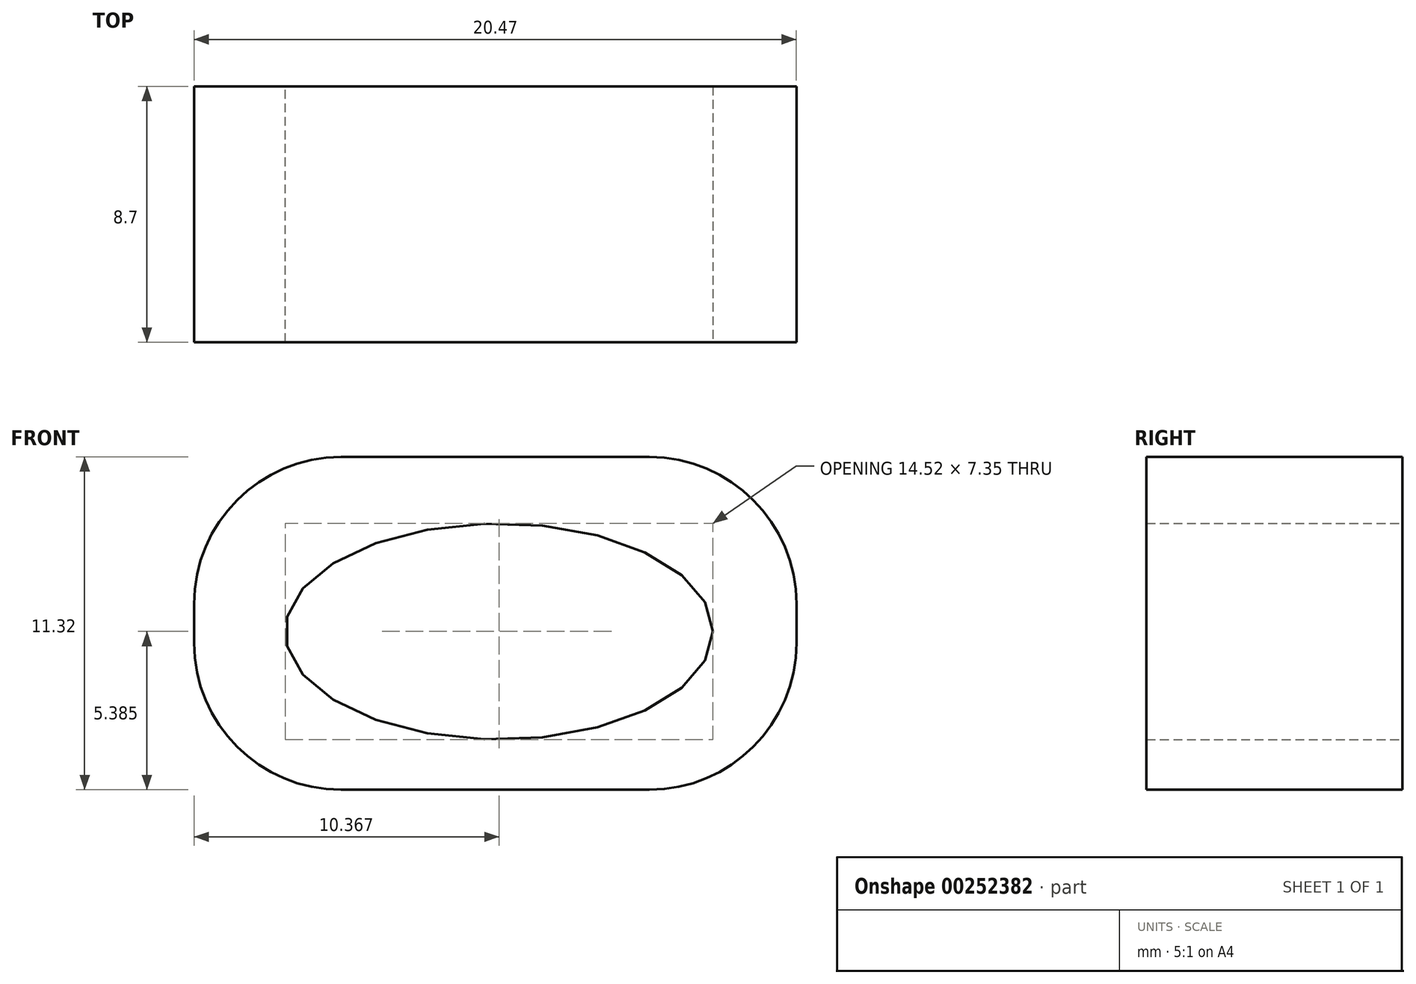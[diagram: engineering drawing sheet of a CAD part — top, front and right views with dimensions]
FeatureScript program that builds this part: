
annotation { "Feature Type Name" : "Feature", "Feature Type Description" : "" }
export const myFeature = defineFeature(function(context is Context, id is Id, definition is map)
    precondition{}
    {
        {
            var Q0;
            Q0=qCreatedBy(makeId("Front.planeOp"),FACE);
            var sketch = newSketch(context, id + "F0", { "sketchPlane" : qUnion([Q0])});
            skLineSegment(sketch, "E0.bottom", {"start": v(-29.85, 38.97) * mm, "end": v(-50.32, 38.97) * mm});
            skLineSegment(sketch, "E0.top", {"start": v(-29.85, 50.29) * mm, "end": v(-50.32, 50.29) * mm});
            skLineSegment(sketch, "E0.left", {"start": v(-29.85, 38.97) * mm, "end": v(-29.85, 50.29) * mm});
            skLineSegment(sketch, "E0.right", {"start": v(-50.32, 38.97) * mm, "end": v(-50.32, 50.29) * mm});
            skPoint(sketch, "E0.middle", {"position": v(-40.08, 44.63) * mm});
            skSolve(sketch);
        }
        {
            var Q0;
            Q0=makeQuery(id+"F0.imprint","IMPRINT",FACE,{"disambiguationData":[TD([[makeQuery(id+"F0.imprint","IMPRINT",EDGE,{"derivedFrom":sQuery(id+"F0.wireOp",EDGE,"E0.bottom")}),-1.0]])]});
            extrude(context, id + "F1", {"entities" : qUnion([Q0]), "depth" : 8.7 * mm});
        }
        {
            var Q0;
            Q0=makeQuery(id+"F1.opExtrude","CAP_FACE",FACE,{"disambiguationData":[OSD([sQuery(id+"F0.wireOp",EDGE,"E0.bottom"),sQuery(id+"F0.wireOp",EDGE,"E0.top"),sQuery(id+"F0.wireOp",EDGE,"E0.left"),sQuery(id+"F0.wireOp",EDGE,"E0.right")])],"isStart":false});
            var sketch = newSketch(context, id + "F2", { "sketchPlane" : qUnion([Q0])});
            skEllipse(sketch, "E1", {"center": v(-39.95, 44.36) * mm, "majorRadius": 7.26 * mm, "minorRadius": 3.68 * mm, "majorAxis": v(1, 0)});
            skSolve(sketch);
        }
        {
            var Q0;
            Q0=makeQuery(id+"F2.imprint","IMPRINT",FACE,{"disambiguationData":[TD([[makeQuery(id+"F2.imprint","IMPRINT",EDGE,{"derivedFrom":sQuery(id+"F2.wireOp",EDGE,"E1")}),1.0]])]});
            extrude(context, id + "F3", {"entities" : qUnion([Q0]), "operationType" : NewBodyOperationType.REMOVE, "oppositeDirection" : true, "depth" : 25 * mm});
        }
        {
            var Q0;
            Q0=makeQuery(id+"F1.opExtrude","SWEPT_EDGE",EDGE,{"disambiguationData":[OSD([sQuery(id+"F0.wireOp",EDGE,"E0.top"),sQuery(id+"F0.wireOp",EDGE,"E0.right")])]});
            var Q1;
            Q1=makeQuery(id+"F1.opExtrude","SWEPT_EDGE",EDGE,{"disambiguationData":[OSD([sQuery(id+"F0.wireOp",EDGE,"E0.bottom"),sQuery(id+"F0.wireOp",EDGE,"E0.right")])]});
            var Q2;
            Q2=makeQuery(id+"F1.opExtrude","SWEPT_EDGE",EDGE,{"disambiguationData":[OSD([sQuery(id+"F0.wireOp",EDGE,"E0.bottom"),sQuery(id+"F0.wireOp",EDGE,"E0.left")])]});
            var Q3;
            Q3=makeQuery(id+"F1.opExtrude","SWEPT_EDGE",EDGE,{"disambiguationData":[OSD([sQuery(id+"F0.wireOp",EDGE,"E0.top"),sQuery(id+"F0.wireOp",EDGE,"E0.left")])]});
            fillet(context, id + "F4", {"entities" : qUnion([Q0, Q1, Q2, Q3]), "radius" : 5 * mm, "tangentPropagation" : true, "allowEdgeOverflow" : false});
        }
    });
